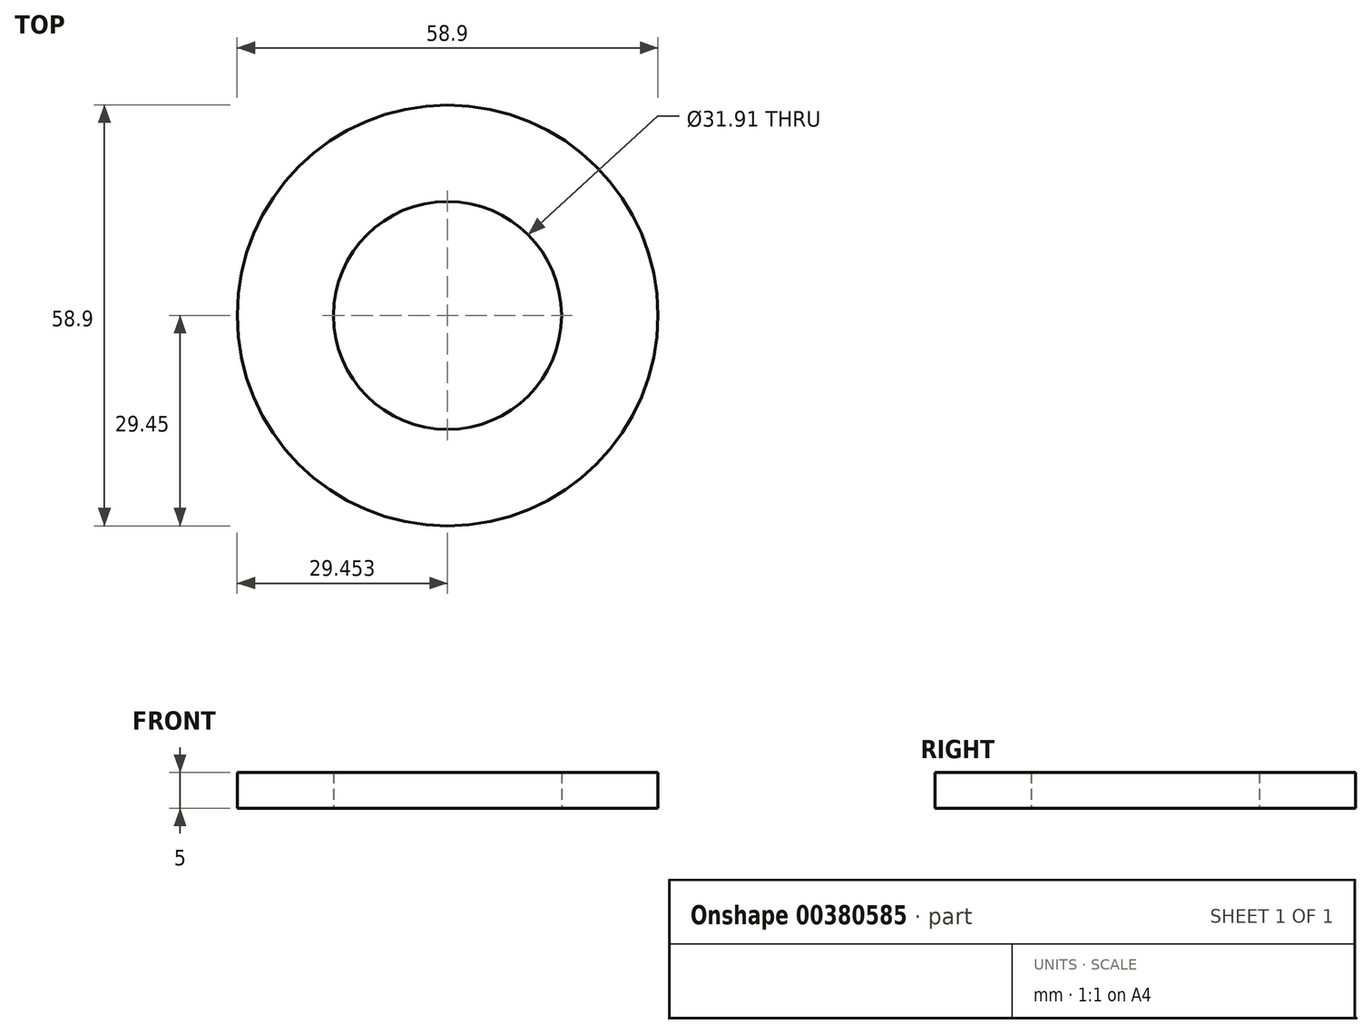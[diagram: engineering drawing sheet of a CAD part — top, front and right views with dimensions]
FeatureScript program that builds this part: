
annotation { "Feature Type Name" : "Feature", "Feature Type Description" : "" }
export const myFeature = defineFeature(function(context is Context, id is Id, definition is map)
    precondition{}
    {
        {
            var Q0;
            Q0=qCreatedBy(makeId("Top.planeOp"),FACE);
            var sketch = newSketch(context, id + "F0", { "sketchPlane" : qUnion([Q0])});
            skCircle(sketch, "E0", {"center": v(-41.4, 0) * mm, "radius": 29.45 * mm});
            skCircle(sketch, "E1", {"center": v(-41.4, 0) * mm, "radius": 15.96 * mm});
            skSolve(sketch);
        }
        {
            var Q0;
            Q0=makeQuery(id+"F0.imprint","IMPRINT",FACE,{"disambiguationData":[TD([[makeQuery(id+"F0.imprint","IMPRINT",EDGE,{"derivedFrom":sQuery(id+"F0.wireOp",EDGE,"E0")}),1.0]])]});
            extrude(context, id + "F1", {"entities" : qUnion([Q0]), "depth" : 5 * mm});
        }
    });
